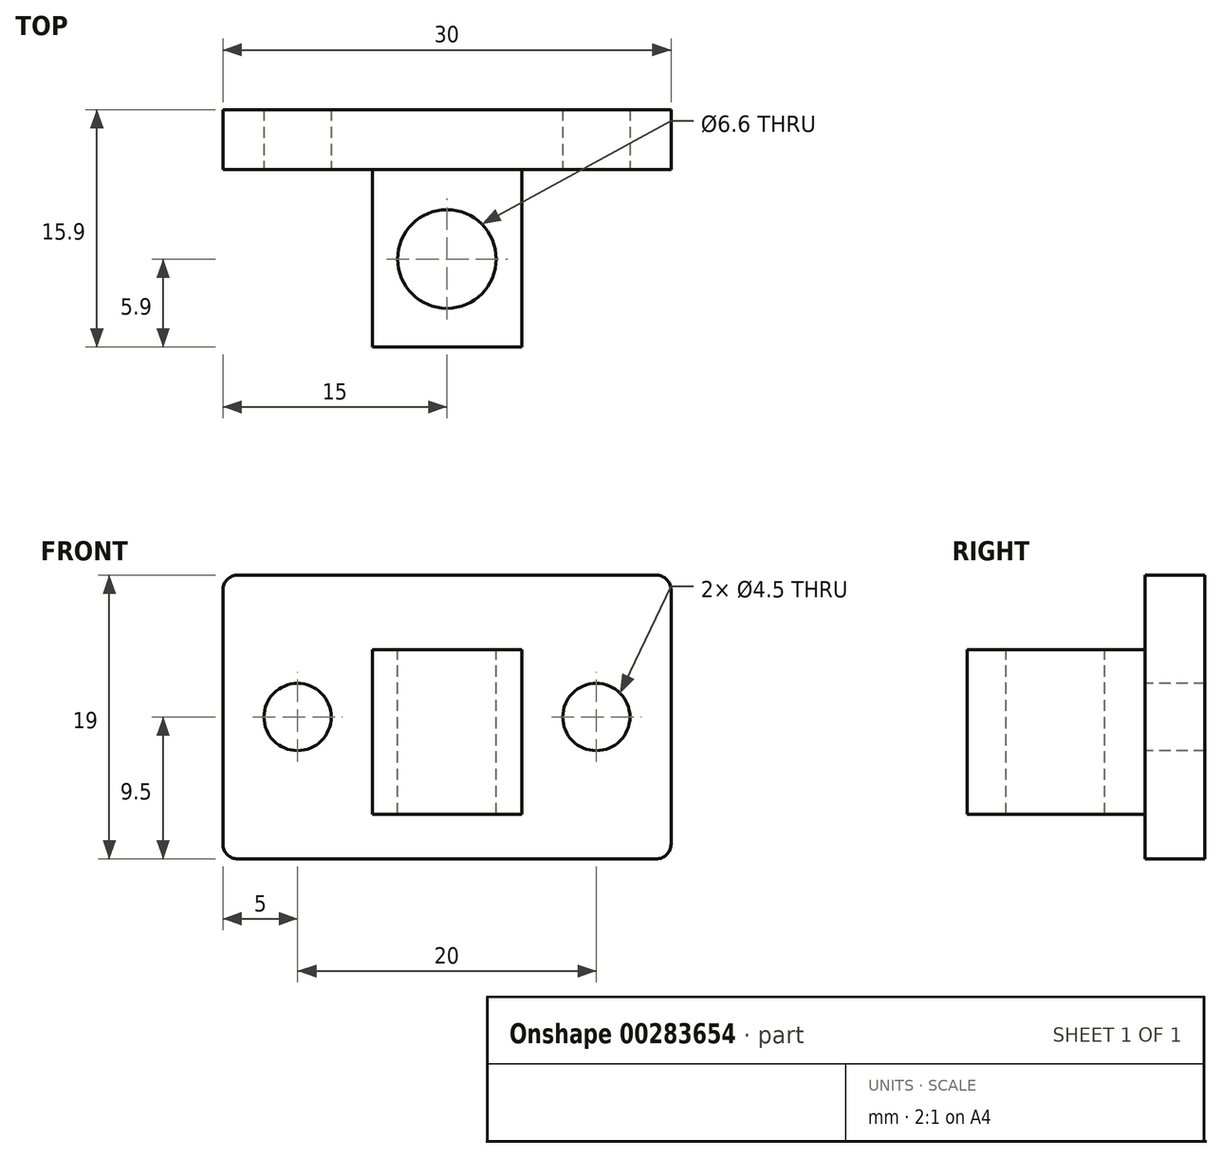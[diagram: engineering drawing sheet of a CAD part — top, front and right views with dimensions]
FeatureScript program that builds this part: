
annotation { "Feature Type Name" : "Feature", "Feature Type Description" : "" }
export const myFeature = defineFeature(function(context is Context, id is Id, definition is map)
    precondition{}
    {
        {
            var Q0;
            Q0=qCreatedBy(makeId("Front.planeOp"),FACE);
            var sketch = newSketch(context, id + "F0", { "sketchPlane" : qUnion([Q0])});
            skLineSegment(sketch, "E0.bottom", {"start": v(0, 0) * mm, "end": v(30, 0) * mm});
            skLineSegment(sketch, "E0.top", {"start": v(0, 19) * mm, "end": v(30, 19) * mm});
            skLineSegment(sketch, "E0.left", {"start": v(0, 0) * mm, "end": v(0, 19) * mm});
            skLineSegment(sketch, "E0.right", {"start": v(30, 0) * mm, "end": v(30, 19) * mm});
            skSolve(sketch);
        }
        {
            var Q0;
            Q0 = qSketchRegion(id + "F0", true);
            extrude(context, id + "F1", {"entities" : qUnion([Q0]), "depth" : 4 * mm});
        }
        {
            var Q0;
            Q0=makeQuery(id+"F1.opExtrude","CAP_FACE",FACE,{"disambiguationData":[OSD([sQuery(id+"F0.wireOp",EDGE,"E0.bottom"),sQuery(id+"F0.wireOp",EDGE,"E0.top"),sQuery(id+"F0.wireOp",EDGE,"E0.left"),sQuery(id+"F0.wireOp",EDGE,"E0.right")])],"isStart":false});
            var sketch = newSketch(context, id + "F2", { "sketchPlane" : qUnion([Q0])});
            skCircle(sketch, "E1", {"center": v(25, 9.5) * mm, "radius": 2.25 * mm});
            skPoint(sketch, "E1.centerSnap0", {"position": v(30, 9.5) * mm});
            skCircle(sketch, "E2", {"center": v(5, 9.5) * mm, "radius": 2.25 * mm});
            skPoint(sketch, "E2.centerSnap0", {"position": v(0, 9.5) * mm});
            skSolve(sketch);
        }
        {
            var Q0;
            Q0 = qSketchRegion(id + "F2", true);
            extrude(context, id + "F3", {"entities" : qUnion([Q0]), "operationType" : NewBodyOperationType.REMOVE, "oppositeDirection" : true, "depth" : 25 * mm});
        }
        {
            var Q0;
            Q0=makeQuery(id+"F1.opExtrude","CAP_FACE",FACE,{"disambiguationData":[OSD([sQuery(id+"F0.wireOp",EDGE,"E0.bottom"),sQuery(id+"F0.wireOp",EDGE,"E0.top"),sQuery(id+"F0.wireOp",EDGE,"E0.left"),sQuery(id+"F0.wireOp",EDGE,"E0.right")])],"isStart":false});
            var sketch = newSketch(context, id + "F4", { "sketchPlane" : qUnion([Q0])});
            skLineSegment(sketch, "E3.bottom", {"start": v(10, 14) * mm, "end": v(20, 14) * mm});
            skLineSegment(sketch, "E3.top", {"start": v(10, 3) * mm, "end": v(20, 3) * mm});
            skLineSegment(sketch, "E3.left", {"start": v(10, 14) * mm, "end": v(10, 3) * mm});
            skLineSegment(sketch, "E3.right", {"start": v(20, 14) * mm, "end": v(20, 3) * mm});
            skSolve(sketch);
        }
        {
            var Q0;
            Q0 = qSketchRegion(id + "F4", true);
            extrude(context, id + "F5", {"entities" : qUnion([Q0]), "operationType" : NewBodyOperationType.ADD, "depth" : 11.9 * mm});
        }
        {
            var Q0;
            Q0=makeQuery(id+"F5.opExtrude","SWEPT_FACE",FACE,{"disambiguationData":[OSD([sQuery(id+"F4.wireOp",EDGE,"E3.bottom")])]});
            var sketch = newSketch(context, id + "F6", { "sketchPlane" : qUnion([Q0])});
            skCircle(sketch, "E4", {"center": v(15, -10) * mm, "radius": 3.3 * mm});
            skPoint(sketch, "E4.centerSnap0", {"position": v(15, -15.9) * mm});
            skSolve(sketch);
        }
        {
            var Q0;
            Q0 = qSketchRegion(id + "F6", true);
            extrude(context, id + "F7", {"entities" : qUnion([Q0]), "operationType" : NewBodyOperationType.REMOVE, "oppositeDirection" : true, "depth" : 25 * mm});
        }
        {
            var Q0;
            Q0=makeQuery(id+"F1.opExtrude","SWEPT_EDGE",EDGE,{"disambiguationData":[OSD([sQuery(id+"F0.wireOp",EDGE,"E0.top"),sQuery(id+"F0.wireOp",EDGE,"E0.left")])]});
            var Q1;
            Q1=makeQuery(id+"F1.opExtrude","SWEPT_EDGE",EDGE,{"disambiguationData":[OSD([sQuery(id+"F0.wireOp",EDGE,"E0.top"),sQuery(id+"F0.wireOp",EDGE,"E0.right")])]});
            var Q2;
            Q2=makeQuery(id+"F1.opExtrude","SWEPT_EDGE",EDGE,{"disambiguationData":[OSD([sQuery(id+"F0.wireOp",EDGE,"E0.bottom"),sQuery(id+"F0.wireOp",EDGE,"E0.right")])]});
            var Q3;
            Q3=makeQuery(id+"F1.opExtrude","SWEPT_EDGE",EDGE,{"disambiguationData":[OSD([sQuery(id+"F0.wireOp",EDGE,"E0.bottom"),sQuery(id+"F0.wireOp",EDGE,"E0.left")])]});
            fillet(context, id + "F8", {"entities" : qUnion([Q0, Q1, Q2, Q3]), "radius" : 1 * mm, "tangentPropagation" : true, "allowEdgeOverflow" : false});
        }
    });
